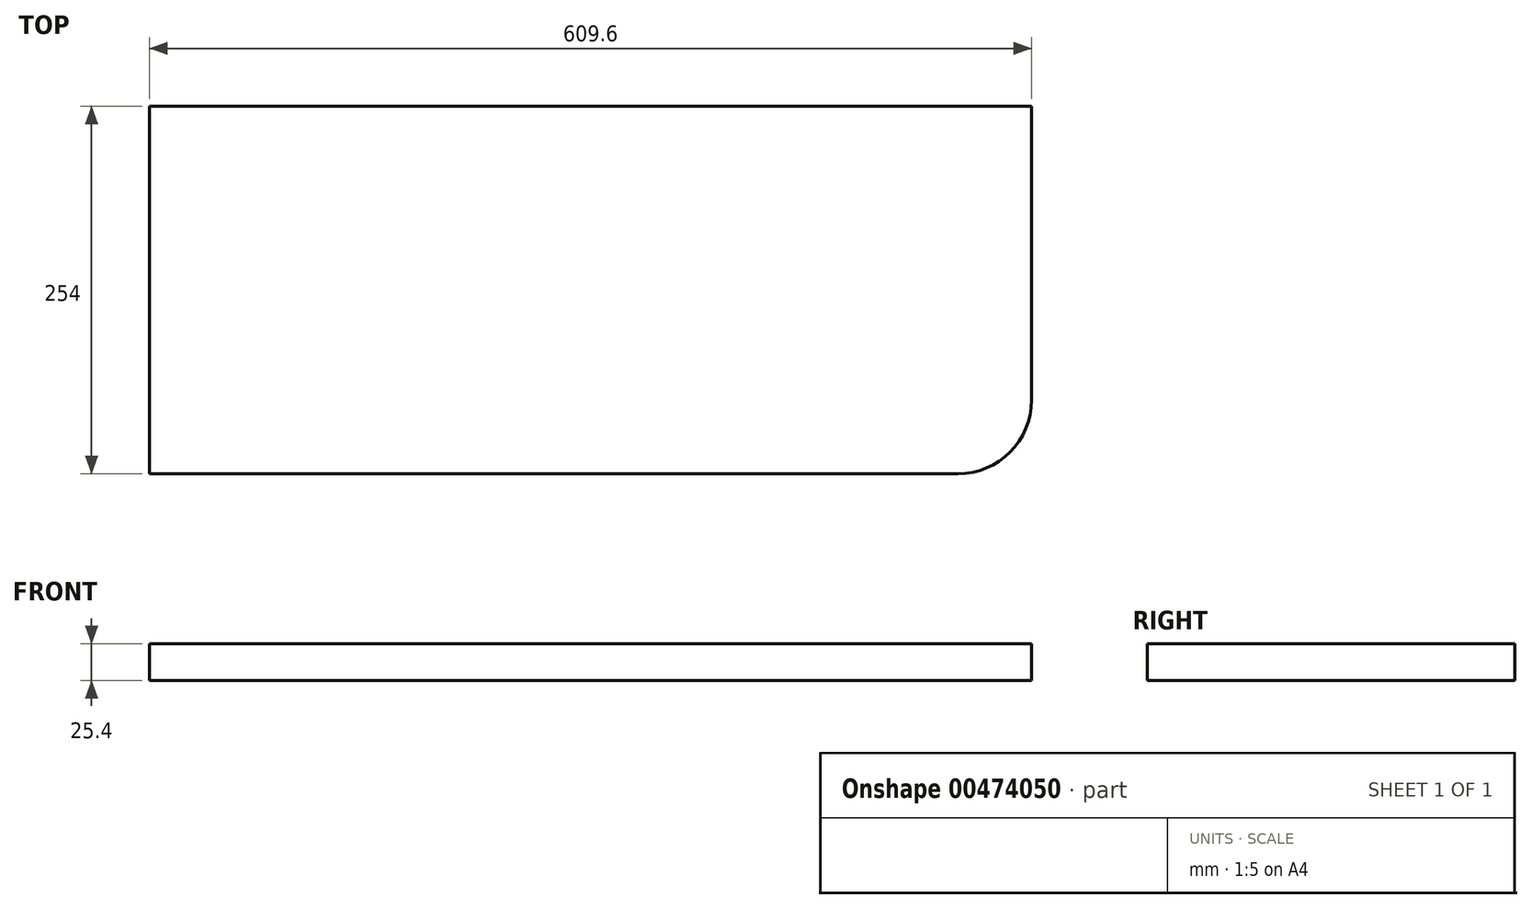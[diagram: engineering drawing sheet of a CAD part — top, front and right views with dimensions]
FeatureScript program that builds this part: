
annotation { "Feature Type Name" : "Feature", "Feature Type Description" : "" }
export const myFeature = defineFeature(function(context is Context, id is Id, definition is map)
    precondition{}
    {
        {
            var Q0;
            Q0=qCreatedBy(makeId("Top.planeOp"),FACE);
            var sketch = newSketch(context, id + "F0", { "sketchPlane" : qUnion([Q0])});
            skLineSegment(sketch, "E0.bottom", {"start": v(0, 0) * mm, "end": v(609.6, 0) * mm});
            skLineSegment(sketch, "E0.top", {"start": v(0, -254) * mm, "end": v(558.8, -254) * mm});
            skLineSegment(sketch, "E0.left", {"start": v(0, 0) * mm, "end": v(0, -254) * mm});
            skLineSegment(sketch, "E0.right", {"start": v(609.6, 0) * mm, "end": v(609.6, -203.2) * mm});
            skPoint(sketch, "E1.visualSharp", {"position": v(609.6, -254) * mm});
            skArc(sketch, "E1.filletArc", {"start": v(558.8, -254) * mm, "mid": v(594.72, -239.12) * mm, "end": v(609.6, -203.2) * mm});
            skSolve(sketch);
        }
        {
            var Q0;
            Q0=makeQuery(id+"F0.imprint","IMPRINT",FACE,{"disambiguationData":[TD([[makeQuery(id+"F0.imprint","IMPRINT",EDGE,{"derivedFrom":sQuery(id+"F0.wireOp",EDGE,"E0.bottom")}),-1.0]])]});
            extrude(context, id + "F1", {"entities" : qUnion([Q0]), "depth" : 25.4 * mm, "offsetDistance" : 25.4 * mm});
        }
    });
